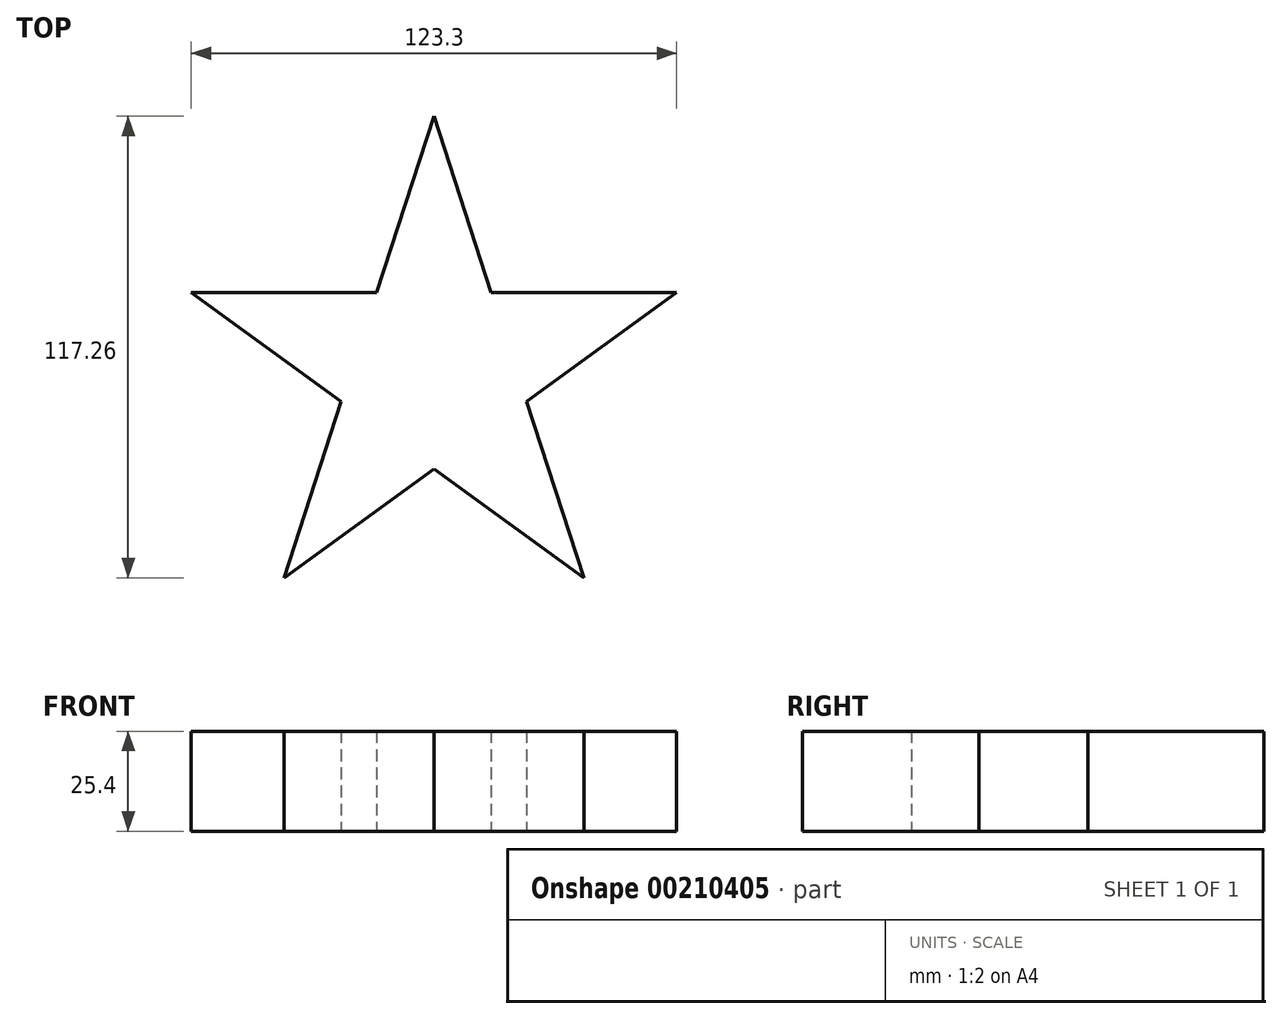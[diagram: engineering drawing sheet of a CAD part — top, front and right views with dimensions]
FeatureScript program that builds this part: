
annotation { "Feature Type Name" : "Feature", "Feature Type Description" : "" }
export const myFeature = defineFeature(function(context is Context, id is Id, definition is map)
    precondition{}
    {
        {
            var Q0;
            Q0=qCreatedBy(makeId("Top.planeOp"),FACE);
            var sketch = newSketch(context, id + "F0", { "sketchPlane" : qUnion([Q0])});
            skCircle(sketch, "E0.cCircle", {"center": v(0, 0) * mm, "radius": 64.82 * mm, "construction": true});
            skLineSegment(sketch, "E0.0", {"start": v(0, 64.82) * mm, "end": v(61.65, 20.03) * mm});
            skLineSegment(sketch, "E0.1", {"start": v(61.65, 20.03) * mm, "end": v(38.1, -52.44) * mm});
            skLineSegment(sketch, "E0.2", {"start": v(38.1, -52.44) * mm, "end": v(-38.1, -52.44) * mm});
            skLineSegment(sketch, "E0.3", {"start": v(-38.1, -52.44) * mm, "end": v(-61.65, 20.03) * mm});
            skLineSegment(sketch, "E0.4", {"start": v(-61.65, 20.03) * mm, "end": v(0, 64.82) * mm});
            skLineSegment(sketch, "E1", {"start": v(0, 64.82) * mm, "end": v(-38.1, -52.44) * mm});
            skLineSegment(sketch, "E2", {"start": v(0, 64.82) * mm, "end": v(38.1, -52.44) * mm});
            skLineSegment(sketch, "E3", {"start": v(-61.65, 20.03) * mm, "end": v(38.1, -52.44) * mm});
            skLineSegment(sketch, "E4", {"start": v(-61.65, 20.03) * mm, "end": v(61.65, 20.03) * mm});
            skLineSegment(sketch, "E5", {"start": v(-38.1, -52.44) * mm, "end": v(61.65, 20.03) * mm});
            skSolve(sketch);
        }
        {
            var Q0;
            {var subQ1=sQuery(id+"F0.wireOp",EDGE,"E1");var subQ3=sQuery(id+"F0.wireOp",EDGE,"E4");var subQ4=makeQuery(id+"F0.imprint","INTERSECT",VERTEX,{"derivedFrom":[subQ1,subQ3]});Q0=makeQuery(id+"F0.imprint","IMPRINT",FACE,{"disambiguationData":[TD([[makeQuery(id+"F0.imprint","IMPRINT",EDGE,{"disambiguationData":[TD([[subQ4,-1.0]])],"derivedFrom":subQ3}),1.0]])]});}
            var Q1;
            {var subQ0=sQuery(id+"F0.wireOp",EDGE,"E4");var subQ1=sQuery(id+"F0.wireOp",EDGE,"E1");var subQ2=makeQuery(id+"F0.imprint","INTERSECT",VERTEX,{"derivedFrom":[subQ1,subQ0]});Q1=makeQuery(id+"F0.imprint","IMPRINT",FACE,{"disambiguationData":[TD([[makeQuery(id+"F0.imprint","IMPRINT",EDGE,{"disambiguationData":[TD([[subQ2,-1.0]])],"derivedFrom":subQ1}),-1.0]])]});}
            var Q2;
            {var subQ1=sQuery(id+"F0.wireOp",EDGE,"E1");var subQ3=sQuery(id+"F0.wireOp",EDGE,"E3");var subQ4=makeQuery(id+"F0.imprint","INTERSECT",VERTEX,{"derivedFrom":[subQ1,subQ3]});Q2=makeQuery(id+"F0.imprint","IMPRINT",FACE,{"disambiguationData":[TD([[makeQuery(id+"F0.imprint","IMPRINT",EDGE,{"disambiguationData":[TD([[subQ4,-1.0]])],"derivedFrom":subQ3}),-1.0]])]});}
            var Q3;
            {var subQ0=sQuery(id+"F0.wireOp",EDGE,"E4");var subQ1=sQuery(id+"F0.wireOp",EDGE,"E2");var subQ2=makeQuery(id+"F0.imprint","INTERSECT",VERTEX,{"derivedFrom":[subQ1,subQ0]});Q3=makeQuery(id+"F0.imprint","IMPRINT",FACE,{"disambiguationData":[TD([[makeQuery(id+"F0.imprint","IMPRINT",EDGE,{"disambiguationData":[TD([[subQ2,-1.0]])],"derivedFrom":subQ1}),1.0]])]});}
            var Q4;
            {var subQ1=sQuery(id+"F0.wireOp",EDGE,"E2");var subQ3=sQuery(id+"F0.wireOp",EDGE,"E5");var subQ4=makeQuery(id+"F0.imprint","INTERSECT",VERTEX,{"derivedFrom":[subQ1,subQ3]});Q4=makeQuery(id+"F0.imprint","IMPRINT",FACE,{"disambiguationData":[TD([[makeQuery(id+"F0.imprint","IMPRINT",EDGE,{"disambiguationData":[TD([[subQ4,1.0]])],"derivedFrom":subQ3}),-1.0]])]});}
            var Q5;
            {var subQ0=sQuery(id+"F0.wireOp",EDGE,"E4");var subQ1=sQuery(id+"F0.wireOp",EDGE,"E1");var subQ2=makeQuery(id+"F0.imprint","INTERSECT",VERTEX,{"derivedFrom":[subQ1,subQ0]});Q5=makeQuery(id+"F0.imprint","IMPRINT",FACE,{"disambiguationData":[TD([[makeQuery(id+"F0.imprint","IMPRINT",EDGE,{"disambiguationData":[TD([[subQ2,-1.0]])],"derivedFrom":subQ1}),1.0]])]});}
            extrude(context, id + "F1", {"entities" : qUnion([Q0, Q1, Q2, Q3, Q4, Q5]), "depth" : 25.4 * mm});
        }
    });
